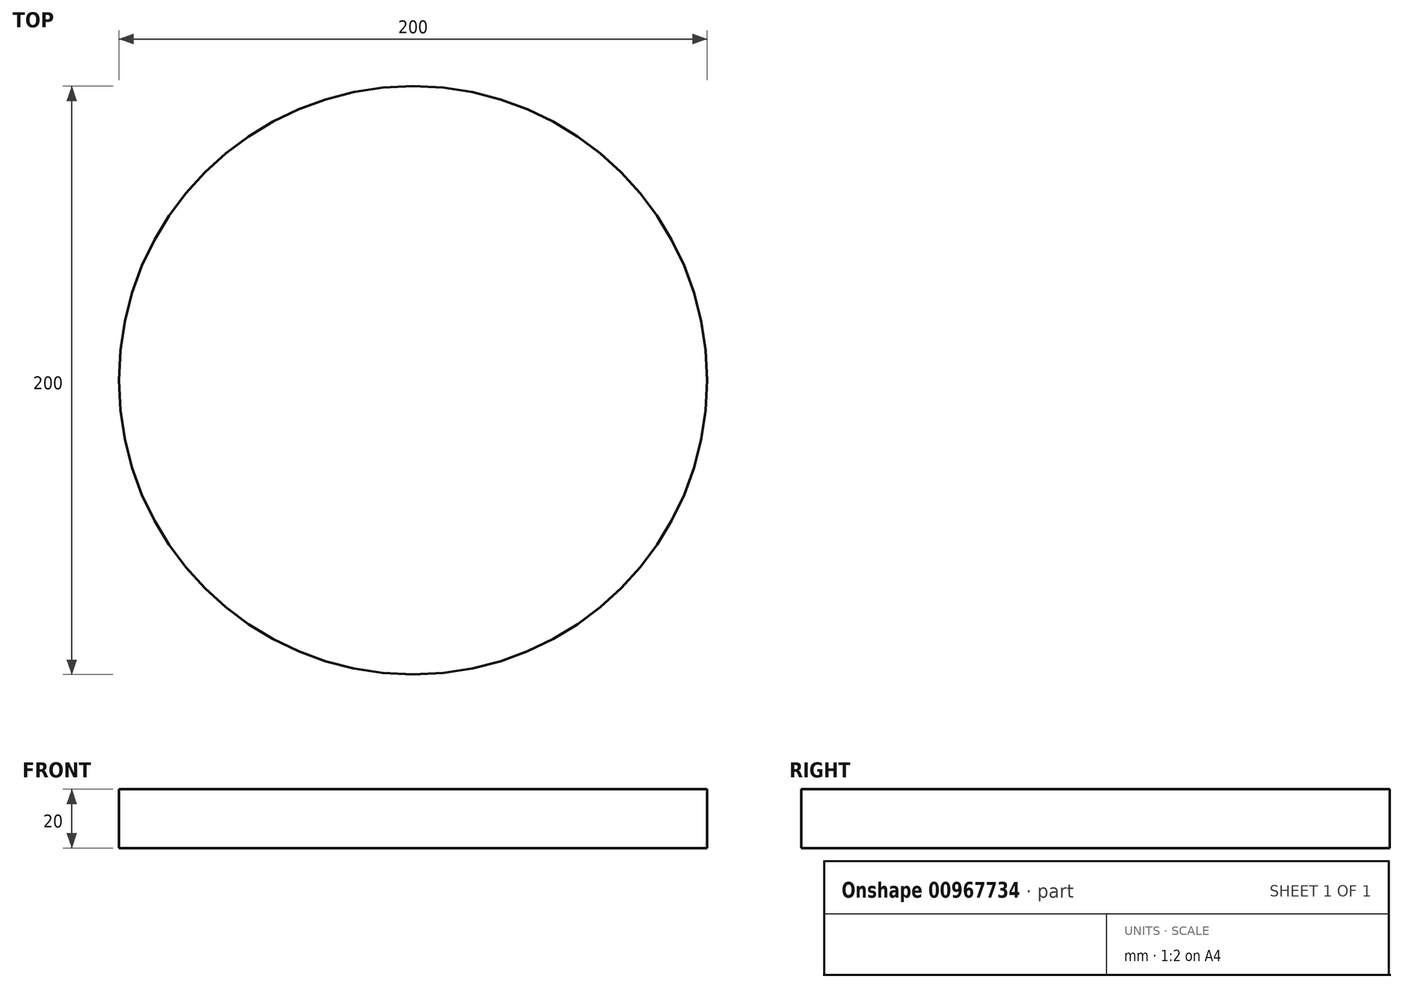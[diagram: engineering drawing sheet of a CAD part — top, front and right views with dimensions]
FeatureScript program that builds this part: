
annotation { "Feature Type Name" : "Feature", "Feature Type Description" : "" }
export const myFeature = defineFeature(function(context is Context, id is Id, definition is map)
    precondition{}
    {
        {
            var Q0;
            Q0=qCreatedBy(makeId("Front.planeOp"),FACE);
            var sketch = newSketch(context, id + "F0", { "sketchPlane" : qUnion([Q0])});
            skLineSegment(sketch, "E0", {"start": v(0, 0) * mm, "end": v(-100, 0) * mm});
            skLineSegment(sketch, "E1", {"start": v(-100, 0) * mm, "end": v(-100, 20) * mm});
            skLineSegment(sketch, "E2", {"start": v(-100, 20) * mm, "end": v(0, 20) * mm});
            skLineSegment(sketch, "E3", {"start": v(0, 20) * mm, "end": v(0, 0) * mm});
            skSolve(sketch);
        }
        {
            var Q0;
            Q0=makeQuery(id+"F0.imprint","IMPRINT",FACE,{"disambiguationData":[TD([[makeQuery(id+"F0.imprint","IMPRINT",EDGE,{"derivedFrom":sQuery(id+"F0.wireOp",EDGE,"E0")}),-1.0]])]});
            var Q1;
            Q1=sQuery(id+"F0.wireOp",EDGE,"E3");
            revolve(context, id + "F1", {"surfaceOperationType" : NewSurfaceOperationType.NEW, "entities" : qUnion([Q0]), "axis" : qUnion([Q1]), "revolveType" : RevolveType.FULL});
        }
    });
